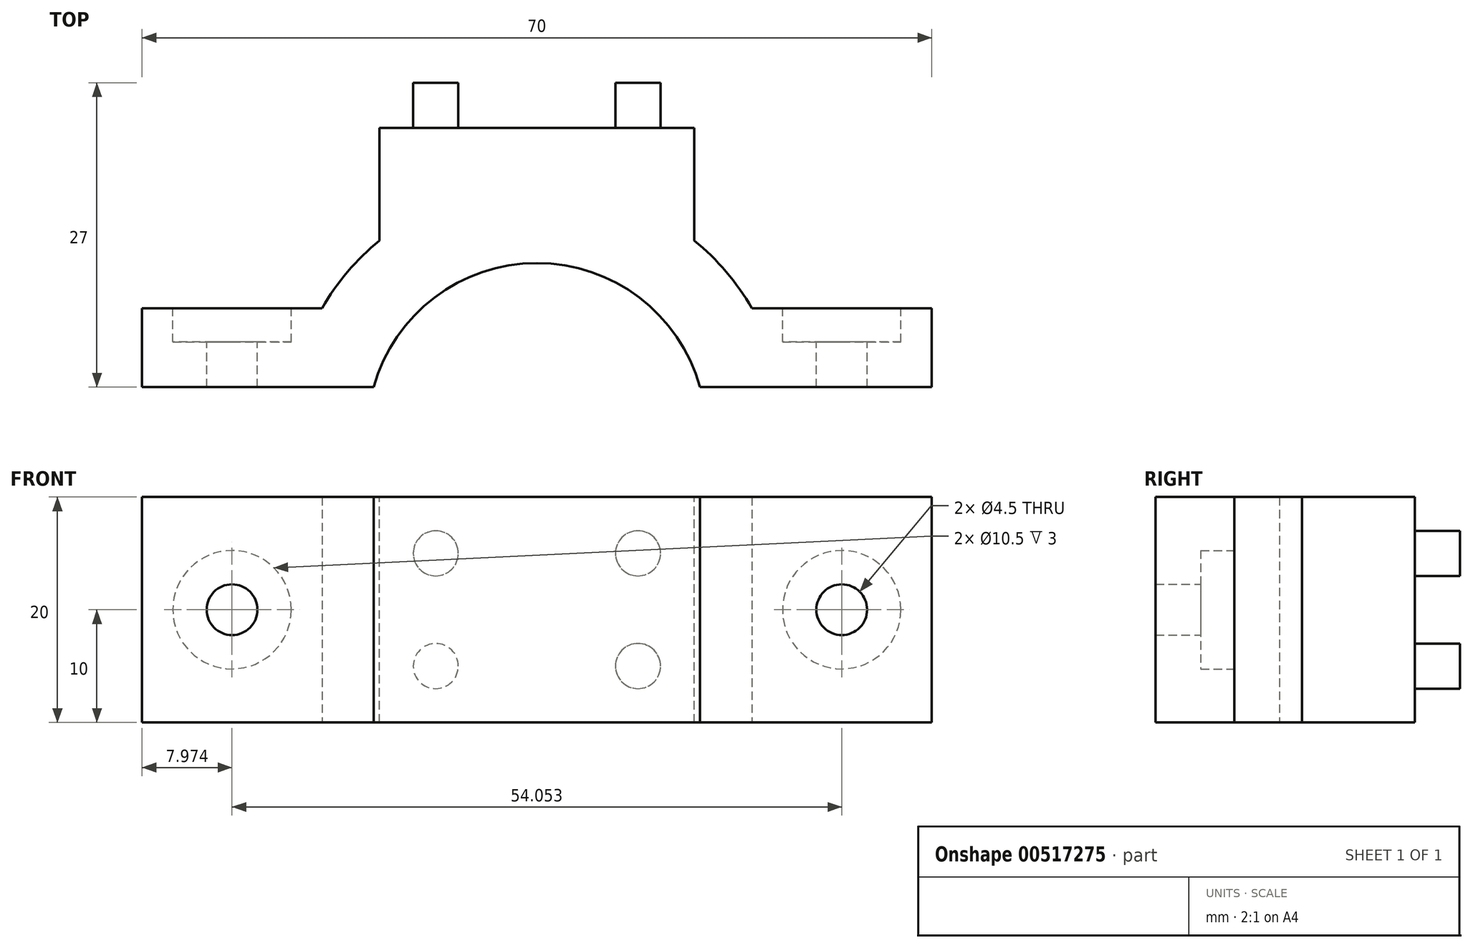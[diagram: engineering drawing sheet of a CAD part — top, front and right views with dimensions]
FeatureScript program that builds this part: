
annotation { "Feature Type Name" : "Feature", "Feature Type Description" : "" }
export const myFeature = defineFeature(function(context is Context, id is Id, definition is map)
    precondition{}
    {
        {
            var Q0;
            Q0=qCreatedBy(makeId("Top.planeOp"),FACE);
            var sketch = newSketch(context, id + "F0", { "sketchPlane" : qUnion([Q0])});
            skLineSegment(sketch, "E0", {"start": v(-35, 0) * mm, "end": v(-14.46, 0) * mm});
            skLineSegment(sketch, "E1.MirrorCS", {"start": v(35, 0) * mm, "end": v(14.46, 0) * mm});
            skArc(sketch, "E2", {"start": v(14.46, 0) * mm, "mid": v(0, 11) * mm, "end": v(-14.46, 0) * mm});
            skArc(sketch, "E3.0", {"start": v(19.05, 7) * mm, "mid": v(0, 18) * mm, "end": v(-19.05, 7) * mm});
            skLineSegment(sketch, "E4.0", {"start": v(-35, 7) * mm, "end": v(-19.05, 7) * mm});
            skLineSegment(sketch, "E5.MirrorCS", {"start": v(35, 7) * mm, "end": v(19.05, 7) * mm});
            skLineSegment(sketch, "E6.MirrorCS", {"start": v(35, 7) * mm, "end": v(35, 0) * mm});
            skLineSegment(sketch, "E7", {"start": v(-35, 7) * mm, "end": v(-35, 0) * mm});
            skSolve(sketch);
        }
        {
            var Q0;
            Q0=qSketchRegion(id+"F0",true);
            extrude(context, id + "F1", {"entities" : qUnion([Q0]), "endBound" : BoundingType.SYMMETRIC, "depth" : 20 * mm, "offsetDistance" : 25 * mm});
        }
        {
            var Q0;
            Q0=makeQuery(id+"F1.opExtrude","SWEPT_FACE",FACE,{"disambiguationData":[OSD([sQuery(id+"F0.wireOp",EDGE,"E5.MirrorCS")])]});
            var sketch = newSketch(context, id + "F2", { "sketchPlane" : qUnion([Q0])});
            skCircle(sketch, "E8", {"center": v(-27.03, 0) * mm, "radius": 2.25 * mm});
            skLineSegment(sketch, "E9", {"start": v(-27.03, 10) * mm, "end": v(-27.03, -10) * mm, "construction": true});
            skCircle(sketch, "E10.MirrorC", {"center": v(27.03, 0) * mm, "radius": 2.25 * mm});
            skSolve(sketch);
        }
        {
            var Q0;
            Q0=qSketchRegion(id+"F2",true);
            extrude(context, id + "F3", {"entities" : qUnion([Q0]), "operationType" : NewBodyOperationType.REMOVE, "oppositeDirection" : true, "depth" : 25 * mm, "offsetDistance" : 25 * mm});
        }
        {
            var Q0;
            Q0=makeQuery(id+"F1.opExtrude","SWEPT_FACE",FACE,{"disambiguationData":[OSD([sQuery(id+"F0.wireOp",EDGE,"E4.0")])]});
            var sketch = newSketch(context, id + "F4", { "sketchPlane" : qUnion([Q0])});
            skCircle(sketch, "E11.0", {"center": v(27.03, 0) * mm, "radius": 2.25 * mm});
            skCircle(sketch, "E12.0", {"center": v(27.03, 0) * mm, "radius": 5.25 * mm});
            skCircle(sketch, "E13.MirrorC", {"center": v(-27.03, 0) * mm, "radius": 5.25 * mm});
            skSolve(sketch);
        }
        {
            var Q0;
            Q0 = qSketchRegion(id + "F4", true);
            extrude(context, id + "F5", {"entities" : qUnion([Q0]), "operationType" : NewBodyOperationType.REMOVE, "oppositeDirection" : true, "depth" : 3 * mm, "offsetDistance" : 25 * mm});
        }
        {
            var Q0;
            Q0=makeQuery(id+"F1.opExtrude","CAP_FACE",FACE,{"disambiguationData":[OSD([sQuery(id+"F0.wireOp",EDGE,"E0"),sQuery(id+"F0.wireOp",EDGE,"E1.MirrorCS"),sQuery(id+"F0.wireOp",EDGE,"E2"),sQuery(id+"F0.wireOp",EDGE,"E3.0"),sQuery(id+"F0.wireOp",EDGE,"E4.0"),sQuery(id+"F0.wireOp",EDGE,"E5.MirrorCS"),sQuery(id+"F0.wireOp",EDGE,"E6.MirrorCS"),sQuery(id+"F0.wireOp",EDGE,"E7")])],"isStart":false});
            var sketch = newSketch(context, id + "F6", { "sketchPlane" : qUnion([Q0])});
            skLineSegment(sketch, "E14.bottom", {"start": v(-13.96, 13) * mm, "end": v(13.96, 13) * mm});
            skLineSegment(sketch, "E14.top", {"start": v(-13.96, 23) * mm, "end": v(13.96, 23) * mm});
            skLineSegment(sketch, "E14.left", {"start": v(-13.96, 13) * mm, "end": v(-13.96, 23) * mm});
            skLineSegment(sketch, "E14.right", {"start": v(13.96, 13) * mm, "end": v(13.96, 23) * mm});
            skLineSegment(sketch, "E15", {"start": v(0, 23) * mm, "end": v(0, 13) * mm, "construction": true});
            skSolve(sketch);
        }
        {
            var Q0;
            Q0 = qSketchRegion(id + "F6", true);
            extrude(context, id + "F7", {"entities" : qUnion([Q0]), "operationType" : NewBodyOperationType.ADD, "oppositeDirection" : true, "depth" : 20 * mm, "offsetDistance" : 25 * mm});
        }
        {
            var Q0;
            Q0=makeQuery(id+"F7.opExtrude","SWEPT_FACE",FACE,{"disambiguationData":[OSD([sQuery(id+"F6.wireOp",EDGE,"E14.top")])]});
            var sketch = newSketch(context, id + "F8", { "sketchPlane" : qUnion([Q0])});
            skLineSegment(sketch, "E16.0", {"start": v(8.96, 5) * mm, "end": v(-8.96, 5) * mm, "construction": true});
            skLineSegment(sketch, "E16.1", {"start": v(8.96, -5) * mm, "end": v(8.96, 5) * mm, "construction": true});
            skLineSegment(sketch, "E16.2", {"start": v(-8.96, -5) * mm, "end": v(8.96, -5) * mm, "construction": true});
            skLineSegment(sketch, "E16.3", {"start": v(-8.96, 5) * mm, "end": v(-8.96, -5) * mm, "construction": true});
            skCircle(sketch, "E17", {"center": v(8.96, -5) * mm, "radius": 2 * mm});
            skCircle(sketch, "E18.MirrorC", {"center": v(-8.96, -5) * mm, "radius": 2 * mm});
            skCircle(sketch, "E19.MirrorC", {"center": v(8.96, 5) * mm, "radius": 2 * mm});
            skCircle(sketch, "E20.MirrorC", {"center": v(-8.96, 5) * mm, "radius": 2 * mm});
            skSolve(sketch);
        }
        {
            var Q0;
            Q0 = qSketchRegion(id + "F8", true);
            extrude(context, id + "F9", {"entities" : qUnion([Q0]), "operationType" : NewBodyOperationType.ADD, "depth" : 4 * mm, "offsetDistance" : 25 * mm});
        }
    });
